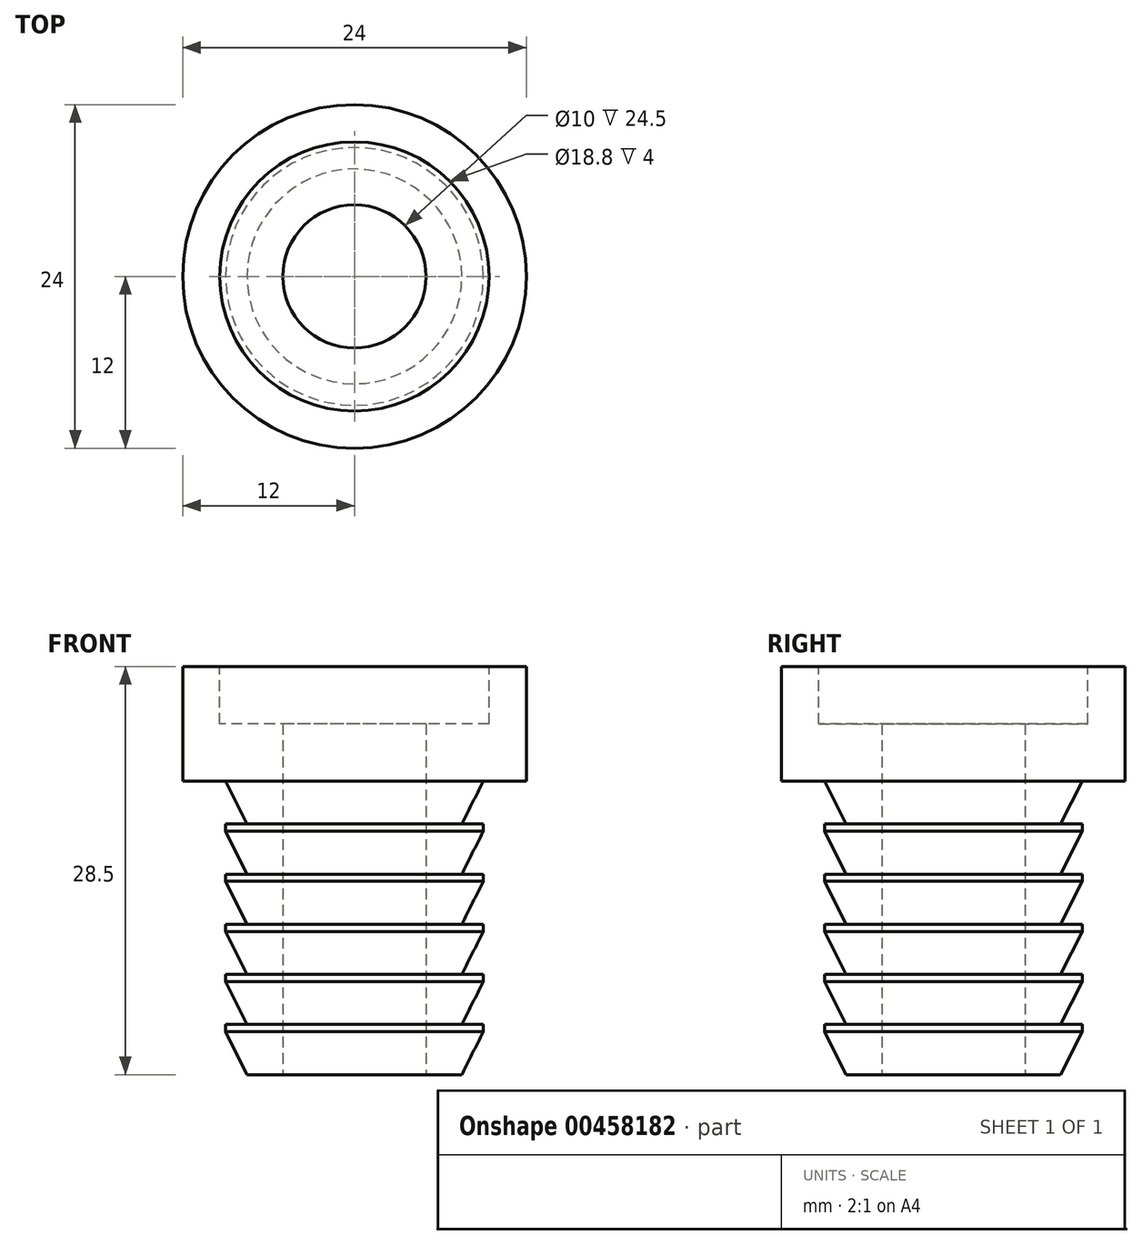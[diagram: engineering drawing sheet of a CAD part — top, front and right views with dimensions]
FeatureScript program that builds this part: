
annotation { "Feature Type Name" : "Feature", "Feature Type Description" : "" }
export const myFeature = defineFeature(function(context is Context, id is Id, definition is map)
    precondition{}
    {
        {
            var Q0;
            Q0=qCreatedBy(makeId("Top.planeOp"),FACE);
            var sketch = newSketch(context, id + "F0", { "sketchPlane" : qUnion([Q0])});
            skCircle(sketch, "E0", {"center": v(0, 0) * mm, "radius": 5 * mm});
            skCircle(sketch, "E1", {"center": v(0, 0) * mm, "radius": 9 * mm});
            skSolve(sketch);
        }
        {
            var Q0;
            Q0=makeQuery(id+"F0.imprint","IMPRINT",FACE,{"disambiguationData":[TD([[makeQuery(id+"F0.imprint","IMPRINT",EDGE,{"derivedFrom":sQuery(id+"F0.wireOp",EDGE,"E0")}),-1.0]])]});
            extrude(context, id + "F1", {"entities" : qUnion([Q0]), "depth" : 25 * mm, "offsetDistance" : 25 * mm});
        }
        {
            var Q0;
            Q0=qCreatedBy(makeId("Top.planeOp"),FACE);
            cPlane(context, id + "F2", {"entities" : qUnion([Q0]), "cplaneType" : CPlaneType.OFFSET, "offset" : 3.5 * mm, "width" : 150 * mm, "height" : 150 * mm});
        }
        {
            var Q0;
            Q0=qCreatedBy(id+"F2.planeOp",FACE);
            var sketch = newSketch(context, id + "F3", { "sketchPlane" : qUnion([Q0])});
            skCircle(sketch, "E2", {"center": v(0, 0) * mm, "radius": 9 * mm});
            skSolve(sketch);
        }
        {
            var Q0;
            Q0=qCreatedBy(id+"F2.planeOp",FACE);
            cPlane(context, id + "F4", {"entities" : qUnion([Q0]), "cplaneType" : CPlaneType.OFFSET, "offset" : 3.5 * mm, "width" : 150 * mm, "height" : 150 * mm});
        }
        {
            var Q0;
            Q0=qCreatedBy(id+"F4.planeOp",FACE);
            var sketch = newSketch(context, id + "F5", { "sketchPlane" : qUnion([Q0])});
            skCircle(sketch, "E3", {"center": v(0, 0) * mm, "radius": 9 * mm});
            skSolve(sketch);
        }
        {
            var Q0;
            Q0=qCreatedBy(id+"F4.planeOp",FACE);
            cPlane(context, id + "F6", {"entities" : qUnion([Q0]), "cplaneType" : CPlaneType.OFFSET, "offset" : 3.5 * mm, "width" : 150 * mm, "height" : 150 * mm});
        }
        {
            var Q0;
            Q0=qCreatedBy(id+"F6.planeOp",FACE);
            var sketch = newSketch(context, id + "F7", { "sketchPlane" : qUnion([Q0])});
            skCircle(sketch, "E4", {"center": v(0, 0) * mm, "radius": 9 * mm});
            skSolve(sketch);
        }
        {
            var Q0;
            Q0=qCreatedBy(id+"F6.planeOp",FACE);
            cPlane(context, id + "F8", {"entities" : qUnion([Q0]), "cplaneType" : CPlaneType.OFFSET, "offset" : 3.5 * mm, "width" : 150 * mm, "height" : 150 * mm});
        }
        {
            var Q0;
            Q0=qCreatedBy(id+"F8.planeOp",FACE);
            var sketch = newSketch(context, id + "F9", { "sketchPlane" : qUnion([Q0])});
            skCircle(sketch, "E5", {"center": v(0, 0) * mm, "radius": 9 * mm});
            skSolve(sketch);
        }
        {
            var Q0;
            Q0=qCreatedBy(id+"F8.planeOp",FACE);
            cPlane(context, id + "F10", {"entities" : qUnion([Q0]), "cplaneType" : CPlaneType.OFFSET, "offset" : 3.5 * mm, "width" : 150 * mm, "height" : 150 * mm});
        }
        {
            var Q0;
            Q0=qCreatedBy(id+"F10.planeOp",FACE);
            var sketch = newSketch(context, id + "F11", { "sketchPlane" : qUnion([Q0])});
            skCircle(sketch, "E6", {"center": v(0, 0) * mm, "radius": 9 * mm});
            skSolve(sketch);
        }
        {
            var Q0;
            Q0=qCreatedBy(id+"F10.planeOp",FACE);
            cPlane(context, id + "F12", {"entities" : qUnion([Q0]), "cplaneType" : CPlaneType.OFFSET, "offset" : 3.5 * mm, "width" : 150 * mm, "height" : 150 * mm});
        }
        {
            var Q0;
            Q0=qCreatedBy(id+"F12.planeOp",FACE);
            var sketch = newSketch(context, id + "F13", { "sketchPlane" : qUnion([Q0])});
            skCircle(sketch, "E7", {"center": v(0, 0) * mm, "radius": 9 * mm});
            skSolve(sketch);
        }
        {
            var Q0;
            Q0=makeQuery(id+"F1.opExtrude","CAP_FACE",FACE,{"disambiguationData":[OSD([sQuery(id+"F0.wireOp",EDGE,"E0"),sQuery(id+"F0.wireOp",EDGE,"E1")])],"isStart":false});
            var sketch = newSketch(context, id + "F14", { "sketchPlane" : qUnion([Q0])});
            skPoint(sketch, "E8", {"position": v(0, -9) * mm});
            skPoint(sketch, "E9", {"position": v(9, 0) * mm});
            skSolve(sketch);
        }
        {
            var Q0;
            Q0=qCreatedBy(makeId("Front.planeOp"),FACE);
            var sketch = newSketch(context, id + "F15", { "sketchPlane" : qUnion([Q0])});
            skLineSegment(sketch, "E10", {"start": v(9, 21) * mm, "end": v(7.5, 18) * mm});
            skLineSegment(sketch, "E11", {"start": v(7.5, 18) * mm, "end": v(9, 18) * mm});
            skLineSegment(sketch, "E12", {"start": v(9, 18) * mm, "end": v(9, 21) * mm});
            skLineSegment(sketch, "E13.1.0.0", {"start": v(9, 14.5) * mm, "end": v(9, 17.5) * mm});
            skLineSegment(sketch, "E13.1.0.1", {"start": v(7.5, 14.5) * mm, "end": v(9, 14.5) * mm});
            skLineSegment(sketch, "E13.1.0.2", {"start": v(9, 17.5) * mm, "end": v(7.5, 14.5) * mm});
            skLineSegment(sketch, "E13.2.0.0", {"start": v(9, 11) * mm, "end": v(9, 14) * mm});
            skLineSegment(sketch, "E13.2.0.1", {"start": v(7.5, 11) * mm, "end": v(9, 11) * mm});
            skLineSegment(sketch, "E13.2.0.2", {"start": v(9, 14) * mm, "end": v(7.5, 11) * mm});
            skLineSegment(sketch, "E13.3.0.0", {"start": v(9, 7.5) * mm, "end": v(9, 10.5) * mm});
            skLineSegment(sketch, "E13.3.0.1", {"start": v(7.5, 7.5) * mm, "end": v(9, 7.5) * mm});
            skLineSegment(sketch, "E13.3.0.2", {"start": v(9, 10.5) * mm, "end": v(7.5, 7.5) * mm});
            skLineSegment(sketch, "E13.4.0.0", {"start": v(9, 4) * mm, "end": v(9, 7) * mm});
            skLineSegment(sketch, "E13.4.0.1", {"start": v(7.5, 4) * mm, "end": v(9, 4) * mm});
            skLineSegment(sketch, "E13.4.0.2", {"start": v(9, 7) * mm, "end": v(7.5, 4) * mm});
            skLineSegment(sketch, "E13.5.0.0", {"start": v(9, 0.5) * mm, "end": v(9, 3.5) * mm});
            skLineSegment(sketch, "E13.5.0.1", {"start": v(7.5, 0.5) * mm, "end": v(9, 0.5) * mm});
            skLineSegment(sketch, "E13.5.0.2", {"start": v(9, 3.5) * mm, "end": v(7.5, 0.5) * mm});
            skLineSegment(sketch, "E13.direction1", {"start": v(9, 18) * mm, "end": v(9, 14.5) * mm, "construction": true});
            skSolve(sketch);
        }
        {
            var Q0;
            Q0 = qSketchRegion(id + "F15", true);
            var Q1;
            Q1=makeQuery(id+"F1.opExtrude","CAP_EDGE",EDGE,{"disambiguationData":[OSD([sQuery(id+"F0.wireOp",EDGE,"E1")])],"isStart":false});
            revolve(context, id + "F16", {"operationType" : NewBodyOperationType.REMOVE, "entities" : qUnion([Q0]), "axis" : qUnion([Q1]), "revolveType" : RevolveType.FULL, "oppositeDirection" : true});
        }
        {
            var Q0;
            Q0=makeQuery(id+"F1.opExtrude","CAP_FACE",FACE,{"disambiguationData":[OSD([sQuery(id+"F0.wireOp",EDGE,"E0"),sQuery(id+"F0.wireOp",EDGE,"E1")])],"isStart":true});
            extrude(context, id + "F17", {"entities" : qUnion([Q0]), "operationType" : NewBodyOperationType.REMOVE, "oppositeDirection" : true, "depth" : 0.5 * mm, "offsetDistance" : 25 * mm});
        }
        {
            var Q0;
            Q0=makeQuery(id+"F14.imprint","IMPRINT",FACE,{"disambiguationData":[TD([[makeQuery(id+"F14.imprint","IMPRINT",EDGE,{"derivedFrom":makeQuery(id+"F1.opExtrude","CAP_EDGE",EDGE,{"disambiguationData":[OSD([sQuery(id+"F0.wireOp",EDGE,"E0")])],"isStart":false})}),-1.0]])]});
            var sketch = newSketch(context, id + "F18", { "sketchPlane" : qUnion([Q0])});
            skCircle(sketch, "E14", {"center": v(0, 0) * mm, "radius": 12 * mm});
            skSolve(sketch);
        }
        {
            var Q0;
            Q0=makeQuery(id+"F18.imprint","IMPRINT",FACE,{"disambiguationData":[TD([[makeQuery(id+"F18.imprint","IMPRINT",EDGE,{"derivedFrom":sQuery(id+"F18.wireOp",EDGE,"E14")}),1.0]])]});
            extrude(context, id + "F19", {"entities" : qUnion([Q0]), "operationType" : NewBodyOperationType.ADD, "endBound" : BoundingType.SYMMETRIC, "depth" : 8 * mm, "offsetDistance" : 25 * mm});
        }
        {
            var Q0;
            Q0=makeQuery(id+"F19.opExtrude","CAP_FACE",FACE,{"disambiguationData":[OSD([sQuery(id+"F0.wireOp",EDGE,"E1"),sQuery(id+"F18.wireOp",EDGE,"E14")])],"isStart":false});
            var sketch = newSketch(context, id + "F20", { "sketchPlane" : qUnion([Q0])});
            skCircle(sketch, "E15", {"center": v(0, 0) * mm, "radius": 9.4 * mm});
            skSolve(sketch);
        }
        {
            var Q0;
            Q0=makeQuery(id+"F20.imprint","IMPRINT",FACE,{"disambiguationData":[TD([[makeQuery(id+"F20.imprint","IMPRINT",EDGE,{"derivedFrom":sQuery(id+"F20.wireOp",EDGE,"E15")}),1.0]])]});
            var Q1;
            Q1=makeQuery(id+"F1.opExtrude","CAP_FACE",FACE,{"disambiguationData":[OSD([sQuery(id+"F0.wireOp",EDGE,"E0"),sQuery(id+"F0.wireOp",EDGE,"E1")])],"isStart":false});
            extrude(context, id + "F21", {"entities" : qUnion([Q0]), "operationType" : NewBodyOperationType.REMOVE, "endBound" : BoundingType.UP_TO_SURFACE, "oppositeDirection" : true, "depth" : 25 * mm, "endBoundEntityFace" : qUnion([Q1]), "offsetDistance" : 25 * mm});
        }
    });
